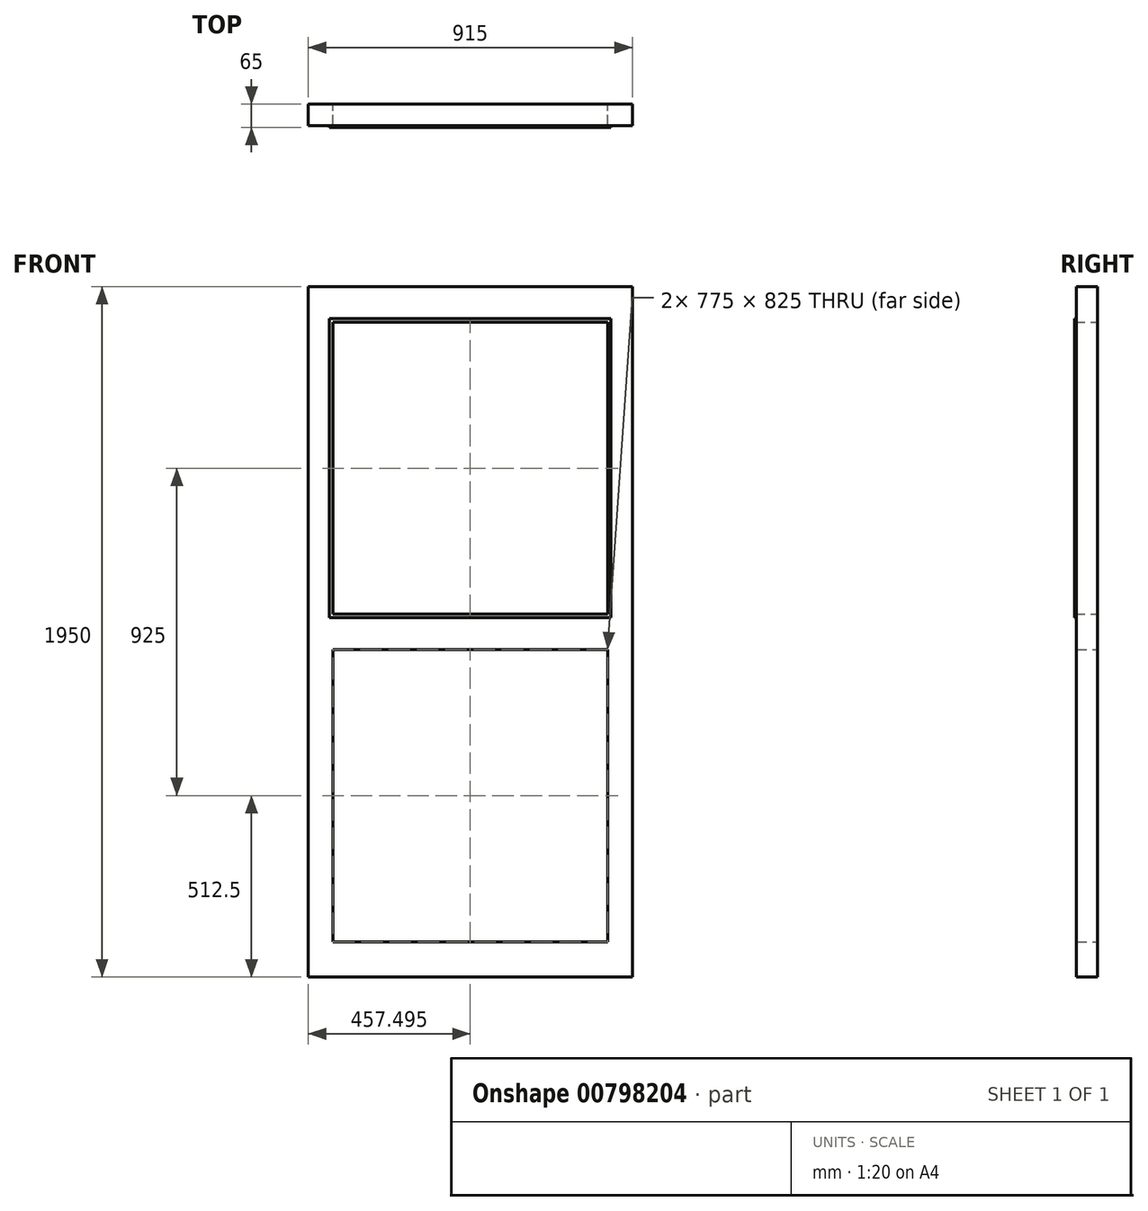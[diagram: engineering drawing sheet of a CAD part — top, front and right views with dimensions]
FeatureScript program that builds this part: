
annotation { "Feature Type Name" : "Feature", "Feature Type Description" : "" }
export const myFeature = defineFeature(function(context is Context, id is Id, definition is map)
    precondition{}
    {
        {
            var Q0;
            Q0=qCreatedBy(makeId("Front.planeOp"),FACE);
            var sketch = newSketch(context, id + "F0", { "sketchPlane" : qUnion([Q0])});
            skLineSegment(sketch, "E0.bottom", {"start": v(-301.4, 951.37) * mm, "end": v(-231.4, 951.37) * mm});
            skLineSegment(sketch, "E0.top", {"start": v(-301.4, -998.63) * mm, "end": v(-231.4, -998.63) * mm});
            skLineSegment(sketch, "E0.left", {"start": v(-301.4, 951.37) * mm, "end": v(-301.4, -998.63) * mm});
            skLineSegment(sketch, "E0.right", {"start": v(-231.4, 951.37) * mm, "end": v(-231.4, -998.63) * mm});
            skLineSegment(sketch, "E1.bottom", {"start": v(543.6, 951.37) * mm, "end": v(613.6, 951.37) * mm});
            skLineSegment(sketch, "E1.top", {"start": v(543.6, -998.63) * mm, "end": v(613.6, -998.63) * mm});
            skLineSegment(sketch, "E1.left", {"start": v(543.6, 951.37) * mm, "end": v(543.6, -998.63) * mm});
            skLineSegment(sketch, "E1.right", {"start": v(613.6, 951.37) * mm, "end": v(613.6, -998.63) * mm});
            skLineSegment(sketch, "E2.bottom", {"start": v(-231.4, 951.37) * mm, "end": v(543.6, 951.37) * mm});
            skLineSegment(sketch, "E2.top", {"start": v(-231.4, 851.37) * mm, "end": v(543.6, 851.37) * mm});
            skLineSegment(sketch, "E2.left", {"start": v(-231.4, 951.37) * mm, "end": v(-231.4, 851.37) * mm});
            skLineSegment(sketch, "E2.right", {"start": v(543.6, 951.37) * mm, "end": v(543.6, 851.37) * mm});
            skLineSegment(sketch, "E3.bottom", {"start": v(-231.4, -998.63) * mm, "end": v(543.6, -998.63) * mm});
            skLineSegment(sketch, "E3.top", {"start": v(-231.4, -898.63) * mm, "end": v(543.6, -898.63) * mm});
            skLineSegment(sketch, "E3.left", {"start": v(-231.4, -998.63) * mm, "end": v(-231.4, -898.63) * mm});
            skLineSegment(sketch, "E3.right", {"start": v(543.6, -998.63) * mm, "end": v(543.6, -898.63) * mm});
            skLineSegment(sketch, "E4.bottom", {"start": v(-231.4, 26.37) * mm, "end": v(543.6, 26.37) * mm});
            skLineSegment(sketch, "E4.top", {"start": v(-231.4, -73.63) * mm, "end": v(543.6, -73.63) * mm});
            skLineSegment(sketch, "E4.left", {"start": v(-231.4, 26.37) * mm, "end": v(-231.4, -73.63) * mm});
            skLineSegment(sketch, "E4.right", {"start": v(543.6, 26.37) * mm, "end": v(543.6, -73.63) * mm});
            skSolve(sketch);
        }
        {
            var Q0;
            Q0=makeQuery(id+"F0.imprint","IMPRINT",FACE,{"disambiguationData":[TD([[makeQuery(id+"F0.imprint","IMPRINT",EDGE,{"derivedFrom":sQuery(id+"F0.wireOp",EDGE,"E0.bottom")}),-1.0]])]});
            var Q1;
            Q1=makeQuery(id+"F0.imprint","IMPRINT",FACE,{"disambiguationData":[TD([[makeQuery(id+"F0.imprint","IMPRINT",EDGE,{"derivedFrom":sQuery(id+"F0.wireOp",EDGE,"E2.bottom")}),-1.0]])]});
            var Q2;
            Q2=makeQuery(id+"F0.imprint","IMPRINT",FACE,{"disambiguationData":[TD([[makeQuery(id+"F0.imprint","IMPRINT",EDGE,{"derivedFrom":sQuery(id+"F0.wireOp",EDGE,"E1.bottom")}),-1.0]])]});
            var Q3;
            Q3=makeQuery(id+"F0.imprint","IMPRINT",FACE,{"disambiguationData":[TD([[makeQuery(id+"F0.imprint","IMPRINT",EDGE,{"derivedFrom":sQuery(id+"F0.wireOp",EDGE,"E4.bottom")}),-1.0]])]});
            var Q4;
            Q4=makeQuery(id+"F0.imprint","IMPRINT",FACE,{"disambiguationData":[TD([[makeQuery(id+"F0.imprint","IMPRINT",EDGE,{"derivedFrom":sQuery(id+"F0.wireOp",EDGE,"E3.bottom")}),1.0]])]});
            extrude(context, id + "F1", {"entities" : qUnion([Q0, Q1, Q2, Q3, Q4]), "depth" : 60 * mm, "offsetDistance" : 25 * mm});
        }
        {
            var Q0;
            Q0=qCreatedBy(makeId("Front.planeOp"),FACE);
            var sketch = newSketch(context, id + "F2", { "sketchPlane" : qUnion([Q0])});
            skLineSegment(sketch, "E5.bottom", {"start": v(-231.4, 16.37) * mm, "end": v(-241.4, 16.37) * mm});
            skLineSegment(sketch, "E5.top", {"start": v(-231.4, 861.37) * mm, "end": v(-241.4, 861.37) * mm});
            skLineSegment(sketch, "E5.left", {"start": v(-231.4, 16.37) * mm, "end": v(-231.4, 861.37) * mm});
            skLineSegment(sketch, "E5.right", {"start": v(-241.4, 16.37) * mm, "end": v(-241.4, 861.37) * mm});
            skLineSegment(sketch, "E6.bottom", {"start": v(-231.4, 16.37) * mm, "end": v(543.6, 16.37) * mm});
            skLineSegment(sketch, "E6.top", {"start": v(-231.4, 26.37) * mm, "end": v(543.6, 26.37) * mm});
            skLineSegment(sketch, "E6.left", {"start": v(-231.4, 16.37) * mm, "end": v(-231.4, 26.37) * mm});
            skLineSegment(sketch, "E6.right", {"start": v(543.6, 16.37) * mm, "end": v(543.6, 26.37) * mm});
            skLineSegment(sketch, "E7.bottom", {"start": v(543.6, 16.37) * mm, "end": v(553.6, 16.37) * mm});
            skLineSegment(sketch, "E7.top", {"start": v(543.6, 861.37) * mm, "end": v(553.6, 861.37) * mm});
            skLineSegment(sketch, "E7.left", {"start": v(543.6, 16.37) * mm, "end": v(543.6, 861.37) * mm});
            skLineSegment(sketch, "E7.right", {"start": v(553.6, 16.37) * mm, "end": v(553.6, 861.37) * mm});
            skLineSegment(sketch, "E8.left", {"start": v(543.6, 861.37) * mm, "end": v(543.6, 851.37) * mm});
            skLineSegment(sketch, "E8.right", {"start": v(-301.4, 861.37) * mm, "end": v(-301.4, 851.37) * mm});
            skLineSegment(sketch, "E9.bottom", {"start": v(543.6, 861.37) * mm, "end": v(-231.4, 861.37) * mm});
            skLineSegment(sketch, "E9.top", {"start": v(543.6, 851.37) * mm, "end": v(-231.4, 851.37) * mm});
            skLineSegment(sketch, "E9.right", {"start": v(-231.4, 861.37) * mm, "end": v(-231.4, 851.37) * mm});
            skSolve(sketch);
        }
        {
            var Q0;
            Q0 = qSketchRegion(id + "F2", true);
            extrude(context, id + "F3", {"entities" : qUnion([Q0]), "operationType" : NewBodyOperationType.ADD, "depth" : 65 * mm, "offsetDistance" : 25 * mm});
        }
    });
